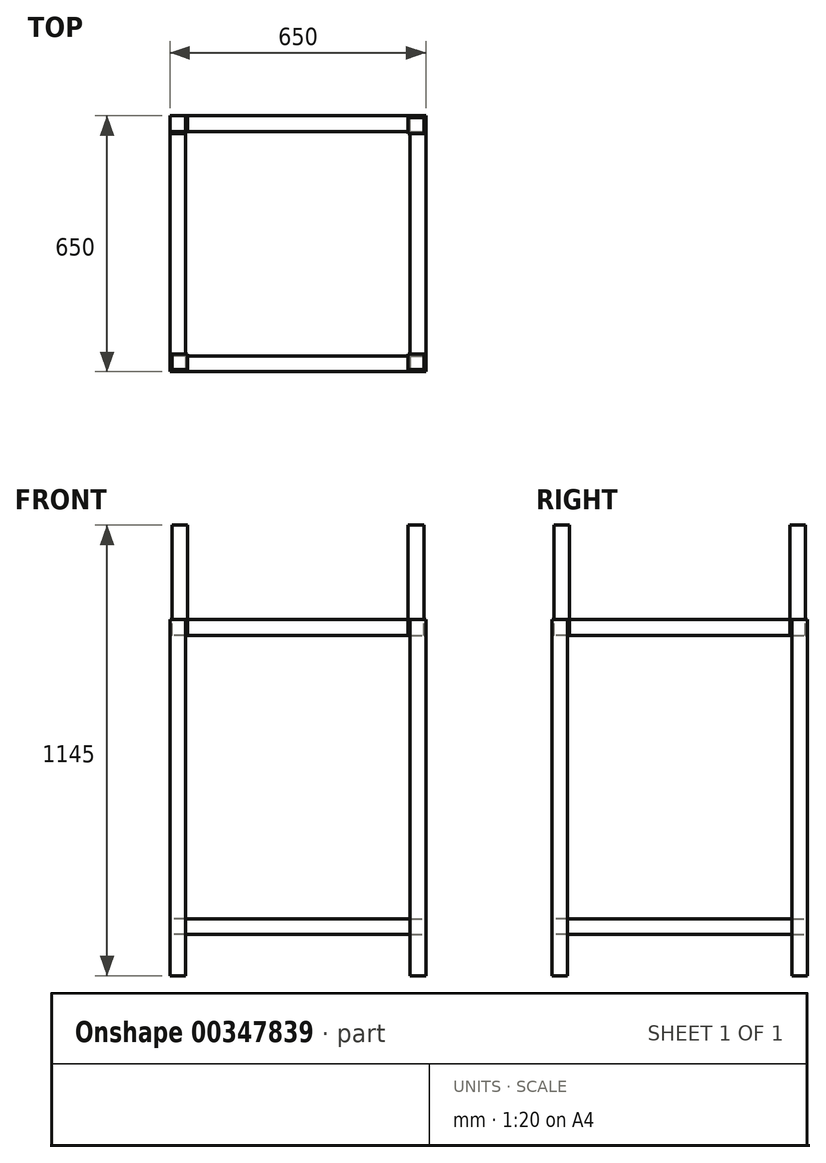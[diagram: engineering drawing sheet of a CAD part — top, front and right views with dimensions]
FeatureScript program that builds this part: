
annotation { "Feature Type Name" : "Feature", "Feature Type Description" : "" }
export const myFeature = defineFeature(function(context is Context, id is Id, definition is map)
    precondition{}
    {
        {
            var Q0;
            Q0=qCreatedBy(makeId("Top.planeOp"),FACE);
            var sketch = newSketch(context, id + "F0", { "sketchPlane" : qUnion([Q0])});
            skLineSegment(sketch, "E0.bottom", {"start": v(325, -325) * mm, "end": v(-325, -325) * mm});
            skLineSegment(sketch, "E0.top", {"start": v(325, 325) * mm, "end": v(-325, 325) * mm});
            skLineSegment(sketch, "E0.left", {"start": v(325, -325) * mm, "end": v(325, 325) * mm});
            skLineSegment(sketch, "E0.right", {"start": v(-325, -325) * mm, "end": v(-325, 325) * mm});
            skPoint(sketch, "E0.middle", {"position": v(0, 0) * mm});
            skLineSegment(sketch, "E1.0", {"start": v(285, 285) * mm, "end": v(-285, 285) * mm});
            skLineSegment(sketch, "E1.1", {"start": v(285, -285) * mm, "end": v(285, 285) * mm});
            skLineSegment(sketch, "E1.2", {"start": v(285, -285) * mm, "end": v(-285, -285) * mm});
            skLineSegment(sketch, "E1.3", {"start": v(-285, -285) * mm, "end": v(-285, 285) * mm});
            skLineSegment(sketch, "E2", {"start": v(-285, 285) * mm, "end": v(-325, 285) * mm});
            skLineSegment(sketch, "E3", {"start": v(-285, 285) * mm, "end": v(-285, 325) * mm});
            skLineSegment(sketch, "E4", {"start": v(285, 285) * mm, "end": v(285, 325) * mm});
            skLineSegment(sketch, "E5", {"start": v(285, 285) * mm, "end": v(325, 285) * mm});
            skLineSegment(sketch, "E6", {"start": v(-285, -285) * mm, "end": v(-325, -285) * mm});
            skLineSegment(sketch, "E7", {"start": v(-285, -285) * mm, "end": v(-285, -325) * mm});
            skLineSegment(sketch, "E8", {"start": v(285, -285) * mm, "end": v(325, -285) * mm});
            skLineSegment(sketch, "E9", {"start": v(285, -285) * mm, "end": v(285, -325) * mm});
            skSolve(sketch);
        }
        {
            var Q0;
            Q0=makeQuery(id+"F0.imprint","IMPRINT",FACE,{"disambiguationData":[TD([[makeQuery(id+"F0.imprint","IMPRINT",EDGE,{"derivedFrom":sQuery(id+"F0.wireOp",EDGE,"E1.0")}),-1.0]])]});
            var Q1;
            Q1=makeQuery(id+"F0.imprint","IMPRINT",FACE,{"disambiguationData":[TD([[makeQuery(id+"F0.imprint","IMPRINT",EDGE,{"derivedFrom":sQuery(id+"F0.wireOp",EDGE,"E1.3")}),1.0]])]});
            var Q2;
            Q2=makeQuery(id+"F0.imprint","IMPRINT",FACE,{"disambiguationData":[TD([[makeQuery(id+"F0.imprint","IMPRINT",EDGE,{"derivedFrom":sQuery(id+"F0.wireOp",EDGE,"E1.1")}),-1.0]])]});
            var Q3;
            Q3=makeQuery(id+"F0.imprint","IMPRINT",FACE,{"disambiguationData":[TD([[makeQuery(id+"F0.imprint","IMPRINT",EDGE,{"derivedFrom":sQuery(id+"F0.wireOp",EDGE,"E1.2")}),1.0]])]});
            extrude(context, id + "F1", {"entities" : qUnion([Q0, Q1, Q2, Q3]), "oppositeDirection" : true, "depth" : 40 * mm});
        }
        {
            var Q0;
            {var subQ4=sQuery(id+"F0.wireOp",EDGE,"E2");Q0=makeQuery(id+"F0.imprint","IMPRINT",FACE,{"disambiguationData":[TD([[makeQuery(id+"F0.imprint","IMPRINT",EDGE,{"derivedFrom":subQ4}),-1.0]])]});}
            var Q1;
            {var subQ3=sQuery(id+"F0.wireOp",EDGE,"E4");Q1=makeQuery(id+"F0.imprint","IMPRINT",FACE,{"disambiguationData":[TD([[makeQuery(id+"F0.imprint","IMPRINT",EDGE,{"derivedFrom":subQ3}),-1.0]])]});}
            var Q2;
            {var subQ4=sQuery(id+"F0.wireOp",EDGE,"E8");Q2=makeQuery(id+"F0.imprint","IMPRINT",FACE,{"disambiguationData":[TD([[makeQuery(id+"F0.imprint","IMPRINT",EDGE,{"derivedFrom":subQ4}),-1.0]])]});}
            var Q3;
            {var subQ4=sQuery(id+"F0.wireOp",EDGE,"E6");Q3=makeQuery(id+"F0.imprint","IMPRINT",FACE,{"disambiguationData":[TD([[makeQuery(id+"F0.imprint","IMPRINT",EDGE,{"derivedFrom":subQ4}),1.0]])]});}
            extrude(context, id + "F2", {"entities" : qUnion([Q0, Q1, Q2, Q3]), "depth" : 760 * mm, "hasSecondDirection" : true, "secondDirectionOppositeDirection" : true, "secondDirectionDepth" : 145 * mm});
        }
        {
            var Q0;
            Q0=makeQuery(id+"F2.opExtrude","CAP_FACE",FACE,{"disambiguationData":[OSD([sQuery(id+"F0.wireOp",EDGE,"E0.top"),sQuery(id+"F0.wireOp",EDGE,"E0.left"),sQuery(id+"F0.wireOp",EDGE,"E4"),sQuery(id+"F0.wireOp",EDGE,"E5")])],"isStart":false});
            var sketch = newSketch(context, id + "F3", { "sketchPlane" : qUnion([Q0])});
            skLineSegment(sketch, "E10.bottom", {"start": v(325, 325) * mm, "end": v(-325, 325) * mm});
            skLineSegment(sketch, "E10.top", {"start": v(325, -325) * mm, "end": v(-325, -325) * mm});
            skLineSegment(sketch, "E10.left", {"start": v(325, 325) * mm, "end": v(325, -325) * mm});
            skLineSegment(sketch, "E10.right", {"start": v(-325, 325) * mm, "end": v(-325, -325) * mm});
            skLineSegment(sketch, "E11.0", {"start": v(285, 285) * mm, "end": v(-285, 285) * mm});
            skLineSegment(sketch, "E11.1", {"start": v(285, 285) * mm, "end": v(285, -285) * mm});
            skLineSegment(sketch, "E11.2", {"start": v(285, -285) * mm, "end": v(-285, -285) * mm});
            skLineSegment(sketch, "E11.3", {"start": v(-285, 285) * mm, "end": v(-285, -285) * mm});
            skLineSegment(sketch, "E12", {"start": v(-285, 285) * mm, "end": v(-285, 325) * mm});
            skLineSegment(sketch, "E13", {"start": v(-285, 285) * mm, "end": v(-325, 285) * mm});
            skLineSegment(sketch, "E14", {"start": v(285, 285) * mm, "end": v(285, 325) * mm});
            skLineSegment(sketch, "E15", {"start": v(285, 285) * mm, "end": v(325, 285) * mm});
            skLineSegment(sketch, "E16", {"start": v(-285, -285) * mm, "end": v(-325, -285) * mm});
            skLineSegment(sketch, "E17", {"start": v(-285, -285) * mm, "end": v(-285, -325) * mm});
            skLineSegment(sketch, "E18", {"start": v(285, -285) * mm, "end": v(325, -285) * mm});
            skLineSegment(sketch, "E19", {"start": v(285, -285) * mm, "end": v(285, -325) * mm});
            skLineSegment(sketch, "E20.0", {"start": v(-280, 280) * mm, "end": v(-280, 325) * mm});
            skLineSegment(sketch, "E20.1", {"start": v(-280, 280) * mm, "end": v(-325, 280) * mm});
            skLineSegment(sketch, "E21.0", {"start": v(-320, 320) * mm, "end": v(-320, 325) * mm});
            skLineSegment(sketch, "E21.1", {"start": v(-320, 320) * mm, "end": v(-325, 320) * mm});
            skLineSegment(sketch, "E22", {"start": v(-320, 320) * mm, "end": v(-280, 320) * mm});
            skLineSegment(sketch, "E23", {"start": v(-320, 320) * mm, "end": v(-320, 280) * mm});
            skLineSegment(sketch, "E24.MirrorCS", {"start": v(320, 320) * mm, "end": v(280, 320) * mm});
            skLineSegment(sketch, "E25.MirrorCS", {"start": v(280, 280) * mm, "end": v(280, 325) * mm});
            skLineSegment(sketch, "E26.MirrorCS", {"start": v(320, 320) * mm, "end": v(320, 280) * mm});
            skLineSegment(sketch, "E27.MirrorCS", {"start": v(280, 280) * mm, "end": v(325, 280) * mm});
            skLineSegment(sketch, "E28.MirrorCS", {"start": v(-325, 325) * mm, "end": v(325, 325) * mm});
            skLineSegment(sketch, "E29.MirrorCS", {"start": v(-320, -320) * mm, "end": v(-280, -320) * mm});
            skLineSegment(sketch, "E30.MirrorCS", {"start": v(-280, -280) * mm, "end": v(-280, -325) * mm});
            skLineSegment(sketch, "E31.MirrorCS", {"start": v(-280, -280) * mm, "end": v(-325, -280) * mm});
            skLineSegment(sketch, "E32.MirrorCS", {"start": v(-320, -320) * mm, "end": v(-320, -280) * mm});
            skLineSegment(sketch, "E33.MirrorCS", {"start": v(-320, -320) * mm, "end": v(-320, -325) * mm});
            skLineSegment(sketch, "E34.MirrorCS", {"start": v(320, -320) * mm, "end": v(280, -320) * mm});
            skLineSegment(sketch, "E35.MirrorCS", {"start": v(320, -320) * mm, "end": v(320, -280) * mm});
            skLineSegment(sketch, "E36.MirrorCS", {"start": v(280, -280) * mm, "end": v(325, -280) * mm});
            skLineSegment(sketch, "E37.MirrorCS", {"start": v(280, -280) * mm, "end": v(280, -325) * mm});
            skSolve(sketch);
        }
        {
            var Q0;
            {var subQ4=sQuery(id+"F3.wireOp",EDGE,"E25.MirrorCS");var subQ6=sQuery(id+"F3.wireOp",EDGE,"E11.0");var subQ7=makeQuery(id+"F3.imprint","INTERSECT",VERTEX,{"derivedFrom":[subQ6,subQ4]});Q0=makeQuery(id+"F3.imprint","IMPRINT",FACE,{"disambiguationData":[TD([[makeQuery(id+"F3.imprint","IMPRINT",EDGE,{"disambiguationData":[TD([[subQ7,-1.0]])],"derivedFrom":subQ6}),-1.0]])]});}
            var Q1;
            {var subQ3=sQuery(id+"F3.wireOp",EDGE,"E20.0");var subQ5=sQuery(id+"F3.wireOp",EDGE,"E22");var subQ7=makeQuery(id+"F3.imprint","INTERSECT",VERTEX,{"derivedFrom":[subQ3,subQ5]});Q1=makeQuery(id+"F3.imprint","IMPRINT",FACE,{"disambiguationData":[TD([[makeQuery(id+"F3.imprint","IMPRINT",EDGE,{"disambiguationData":[TD([[subQ7,1.0]])],"derivedFrom":subQ3}),1.0]])]});}
            var Q2;
            {var subQ0=sQuery(id+"F3.wireOp",EDGE,"E28.MirrorCS");var subQ1=sQuery(id+"F3.wireOp",EDGE,"E12");var subQ2=makeQuery(id+"F3.imprint","INTERSECT",VERTEX,{"derivedFrom":[subQ1,subQ0]});Q2=makeQuery(id+"F3.imprint","IMPRINT",FACE,{"disambiguationData":[TD([[makeQuery(id+"F3.imprint","IMPRINT",EDGE,{"disambiguationData":[TD([[subQ2,1.0]])],"derivedFrom":subQ1}),-1.0]])]});}
            var Q3;
            {var subQ3=sQuery(id+"F3.wireOp",EDGE,"E20.1");var subQ5=sQuery(id+"F3.wireOp",EDGE,"E23");var subQ7=makeQuery(id+"F3.imprint","INTERSECT",VERTEX,{"derivedFrom":[subQ3,subQ5]});Q3=makeQuery(id+"F3.imprint","IMPRINT",FACE,{"disambiguationData":[TD([[makeQuery(id+"F3.imprint","IMPRINT",EDGE,{"disambiguationData":[TD([[subQ7,1.0]])],"derivedFrom":subQ3}),-1.0]])]});}
            var Q4;
            {var subQ0=sQuery(id+"F3.wireOp",EDGE,"E13");var subQ1=sQuery(id+"F3.wireOp",EDGE,"E10.right");var subQ2=makeQuery(id+"F3.imprint","INTERSECT",VERTEX,{"derivedFrom":[subQ1,subQ0]});Q4=makeQuery(id+"F3.imprint","IMPRINT",FACE,{"disambiguationData":[TD([[makeQuery(id+"F3.imprint","IMPRINT",EDGE,{"disambiguationData":[TD([[subQ2,-1.0]])],"derivedFrom":subQ1}),1.0]])]});}
            var Q5;
            {var subQ0=sQuery(id+"F3.wireOp",EDGE,"E20.1");var subQ1=sQuery(id+"F3.wireOp",EDGE,"E10.right");var subQ2=makeQuery(id+"F3.imprint","INTERSECT",VERTEX,{"derivedFrom":[subQ1,subQ0]});Q5=makeQuery(id+"F3.imprint","IMPRINT",FACE,{"disambiguationData":[TD([[makeQuery(id+"F3.imprint","IMPRINT",EDGE,{"disambiguationData":[TD([[subQ2,-1.0]])],"derivedFrom":subQ1}),1.0]])]});}
            var Q6;
            {var subQ3=sQuery(id+"F3.wireOp",EDGE,"E25.MirrorCS");var subQ5=sQuery(id+"F3.wireOp",EDGE,"E24.MirrorCS");var subQ6=makeQuery(id+"F3.imprint","INTERSECT",VERTEX,{"derivedFrom":[subQ3,subQ5]});Q6=makeQuery(id+"F3.imprint","IMPRINT",FACE,{"disambiguationData":[TD([[makeQuery(id+"F3.imprint","IMPRINT",EDGE,{"disambiguationData":[TD([[subQ6,1.0]])],"derivedFrom":subQ3}),-1.0]])]});}
            var Q7;
            {var subQ0=sQuery(id+"F3.wireOp",EDGE,"E28.MirrorCS");var subQ1=sQuery(id+"F3.wireOp",EDGE,"E14");var subQ2=makeQuery(id+"F3.imprint","INTERSECT",VERTEX,{"derivedFrom":[subQ1,subQ0]});Q7=makeQuery(id+"F3.imprint","IMPRINT",FACE,{"disambiguationData":[TD([[makeQuery(id+"F3.imprint","IMPRINT",EDGE,{"disambiguationData":[TD([[subQ2,1.0]])],"derivedFrom":subQ1}),1.0]])]});}
            var Q8;
            {var subQ3=sQuery(id+"F3.wireOp",EDGE,"E27.MirrorCS");var subQ5=sQuery(id+"F3.wireOp",EDGE,"E26.MirrorCS");var subQ7=makeQuery(id+"F3.imprint","INTERSECT",VERTEX,{"derivedFrom":[subQ5,subQ3]});Q8=makeQuery(id+"F3.imprint","IMPRINT",FACE,{"disambiguationData":[TD([[makeQuery(id+"F3.imprint","IMPRINT",EDGE,{"disambiguationData":[TD([[subQ7,1.0]])],"derivedFrom":subQ5}),-1.0]])]});}
            var Q9;
            {var subQ1=sQuery(id+"F3.wireOp",EDGE,"E10.left");var subQ3=sQuery(id+"F3.wireOp",EDGE,"E27.MirrorCS");var subQ4=makeQuery(id+"F3.imprint","INTERSECT",VERTEX,{"derivedFrom":[subQ1,subQ3]});Q9=makeQuery(id+"F3.imprint","IMPRINT",FACE,{"disambiguationData":[TD([[makeQuery(id+"F3.imprint","IMPRINT",EDGE,{"disambiguationData":[TD([[subQ4,1.0]])],"derivedFrom":subQ1}),-1.0]])]});}
            var Q10;
            {var subQ0=sQuery(id+"F3.wireOp",EDGE,"E27.MirrorCS");var subQ2=sQuery(id+"F3.wireOp",EDGE,"E10.left");var subQ3=makeQuery(id+"F3.imprint","INTERSECT",VERTEX,{"derivedFrom":[subQ2,subQ0]});Q10=makeQuery(id+"F3.imprint","IMPRINT",FACE,{"disambiguationData":[TD([[makeQuery(id+"F3.imprint","IMPRINT",EDGE,{"disambiguationData":[TD([[subQ3,-1.0]])],"derivedFrom":subQ2}),-1.0]])]});}
            var Q11;
            {var subQ3=sQuery(id+"F3.wireOp",EDGE,"E36.MirrorCS");var subQ5=sQuery(id+"F3.wireOp",EDGE,"E35.MirrorCS");var subQ6=makeQuery(id+"F3.imprint","INTERSECT",VERTEX,{"derivedFrom":[subQ5,subQ3]});Q11=makeQuery(id+"F3.imprint","IMPRINT",FACE,{"disambiguationData":[TD([[makeQuery(id+"F3.imprint","IMPRINT",EDGE,{"disambiguationData":[TD([[subQ6,1.0]])],"derivedFrom":subQ5}),1.0]])]});}
            var Q12;
            {var subQ0=sQuery(id+"F3.wireOp",EDGE,"E18");var subQ1=sQuery(id+"F3.wireOp",EDGE,"E10.left");var subQ2=makeQuery(id+"F3.imprint","INTERSECT",VERTEX,{"derivedFrom":[subQ1,subQ0]});Q12=makeQuery(id+"F3.imprint","IMPRINT",FACE,{"disambiguationData":[TD([[makeQuery(id+"F3.imprint","IMPRINT",EDGE,{"disambiguationData":[TD([[subQ2,1.0]])],"derivedFrom":subQ1}),-1.0]])]});}
            var Q13;
            {var subQ3=sQuery(id+"F3.wireOp",EDGE,"E37.MirrorCS");var subQ5=sQuery(id+"F3.wireOp",EDGE,"E34.MirrorCS");var subQ7=makeQuery(id+"F3.imprint","INTERSECT",VERTEX,{"derivedFrom":[subQ5,subQ3]});Q13=makeQuery(id+"F3.imprint","IMPRINT",FACE,{"disambiguationData":[TD([[makeQuery(id+"F3.imprint","IMPRINT",EDGE,{"disambiguationData":[TD([[subQ7,1.0]])],"derivedFrom":subQ5}),-1.0]])]});}
            var Q14;
            {var subQ0=sQuery(id+"F3.wireOp",EDGE,"E19");var subQ1=sQuery(id+"F3.wireOp",EDGE,"E10.top");var subQ2=makeQuery(id+"F3.imprint","INTERSECT",VERTEX,{"derivedFrom":[subQ1,subQ0]});Q14=makeQuery(id+"F3.imprint","IMPRINT",FACE,{"disambiguationData":[TD([[makeQuery(id+"F3.imprint","IMPRINT",EDGE,{"disambiguationData":[TD([[subQ2,-1.0]])],"derivedFrom":subQ1}),-1.0]])]});}
            var Q15;
            {var subQ0=sQuery(id+"F3.wireOp",EDGE,"E30.MirrorCS");var subQ6=sQuery(id+"F3.wireOp",EDGE,"E10.top");var subQ7=makeQuery(id+"F3.imprint","INTERSECT",VERTEX,{"derivedFrom":[subQ6,subQ0]});Q15=makeQuery(id+"F3.imprint","IMPRINT",FACE,{"disambiguationData":[TD([[makeQuery(id+"F3.imprint","IMPRINT",EDGE,{"disambiguationData":[TD([[subQ7,1.0]])],"derivedFrom":subQ6}),-1.0]])]});}
            var Q16;
            {var subQ3=sQuery(id+"F3.wireOp",EDGE,"E30.MirrorCS");var subQ5=sQuery(id+"F3.wireOp",EDGE,"E29.MirrorCS");var subQ7=makeQuery(id+"F3.imprint","INTERSECT",VERTEX,{"derivedFrom":[subQ5,subQ3]});Q16=makeQuery(id+"F3.imprint","IMPRINT",FACE,{"disambiguationData":[TD([[makeQuery(id+"F3.imprint","IMPRINT",EDGE,{"disambiguationData":[TD([[subQ7,1.0]])],"derivedFrom":subQ5}),1.0]])]});}
            var Q17;
            {var subQ0=sQuery(id+"F3.wireOp",EDGE,"E17");var subQ1=sQuery(id+"F3.wireOp",EDGE,"E10.top");var subQ2=makeQuery(id+"F3.imprint","INTERSECT",VERTEX,{"derivedFrom":[subQ1,subQ0]});Q17=makeQuery(id+"F3.imprint","IMPRINT",FACE,{"disambiguationData":[TD([[makeQuery(id+"F3.imprint","IMPRINT",EDGE,{"disambiguationData":[TD([[subQ2,1.0]])],"derivedFrom":subQ1}),-1.0]])]});}
            var Q18;
            {var subQ3=sQuery(id+"F3.wireOp",EDGE,"E31.MirrorCS");var subQ5=sQuery(id+"F3.wireOp",EDGE,"E32.MirrorCS");var subQ7=makeQuery(id+"F3.imprint","INTERSECT",VERTEX,{"derivedFrom":[subQ3,subQ5]});Q18=makeQuery(id+"F3.imprint","IMPRINT",FACE,{"disambiguationData":[TD([[makeQuery(id+"F3.imprint","IMPRINT",EDGE,{"disambiguationData":[TD([[subQ7,1.0]])],"derivedFrom":subQ3}),1.0]])]});}
            var Q19;
            {var subQ0=sQuery(id+"F3.wireOp",EDGE,"E16");var subQ1=sQuery(id+"F3.wireOp",EDGE,"E10.right");var subQ2=makeQuery(id+"F3.imprint","INTERSECT",VERTEX,{"derivedFrom":[subQ1,subQ0]});Q19=makeQuery(id+"F3.imprint","IMPRINT",FACE,{"disambiguationData":[TD([[makeQuery(id+"F3.imprint","IMPRINT",EDGE,{"disambiguationData":[TD([[subQ2,1.0]])],"derivedFrom":subQ1}),1.0]])]});}
            extrude(context, id + "F4", {"entities" : qUnion([Q0, Q1, Q2, Q3, Q4, Q5, Q6, Q7, Q8, Q9, Q10, Q11, Q12, Q13, Q14, Q15, Q16, Q17, Q18, Q19]), "oppositeDirection" : true, "depth" : 40 * mm});
        }
        {
            var Q0;
            {var subQ3=sQuery(id+"F3.wireOp",EDGE,"E36.MirrorCS");var subQ5=sQuery(id+"F3.wireOp",EDGE,"E35.MirrorCS");var subQ6=makeQuery(id+"F3.imprint","INTERSECT",VERTEX,{"derivedFrom":[subQ5,subQ3]});Q0=makeQuery(id+"F3.imprint","IMPRINT",FACE,{"disambiguationData":[TD([[makeQuery(id+"F3.imprint","IMPRINT",EDGE,{"disambiguationData":[TD([[subQ6,1.0]])],"derivedFrom":subQ5}),1.0]])]});}
            var Q1;
            {var subQ3=sQuery(id+"F3.wireOp",EDGE,"E35.MirrorCS");var subQ5=sQuery(id+"F3.wireOp",EDGE,"E34.MirrorCS");var subQ6=makeQuery(id+"F3.imprint","INTERSECT",VERTEX,{"derivedFrom":[subQ5,subQ3]});Q1=makeQuery(id+"F3.imprint","IMPRINT",FACE,{"disambiguationData":[TD([[makeQuery(id+"F3.imprint","IMPRINT",EDGE,{"disambiguationData":[TD([[subQ6,-1.0]])],"derivedFrom":subQ5}),-1.0]])]});}
            var Q2;
            {var subQ3=sQuery(id+"F3.wireOp",EDGE,"E37.MirrorCS");var subQ5=sQuery(id+"F3.wireOp",EDGE,"E34.MirrorCS");var subQ7=makeQuery(id+"F3.imprint","INTERSECT",VERTEX,{"derivedFrom":[subQ5,subQ3]});Q2=makeQuery(id+"F3.imprint","IMPRINT",FACE,{"disambiguationData":[TD([[makeQuery(id+"F3.imprint","IMPRINT",EDGE,{"disambiguationData":[TD([[subQ7,1.0]])],"derivedFrom":subQ5}),-1.0]])]});}
            var Q3;
            {var subQ3=sQuery(id+"F3.wireOp",EDGE,"E36.MirrorCS");var subQ5=sQuery(id+"F3.wireOp",EDGE,"E37.MirrorCS");var subQ7=makeQuery(id+"F3.imprint","INTERSECT",VERTEX,{"derivedFrom":[subQ3,subQ5]});Q3=makeQuery(id+"F3.imprint","IMPRINT",FACE,{"disambiguationData":[TD([[makeQuery(id+"F3.imprint","IMPRINT",EDGE,{"disambiguationData":[TD([[subQ7,-1.0]])],"derivedFrom":subQ3}),-1.0]])]});}
            var Q4;
            {var subQ3=sQuery(id+"F3.wireOp",EDGE,"E24.MirrorCS");var subQ5=sQuery(id+"F3.wireOp",EDGE,"E26.MirrorCS");var subQ7=makeQuery(id+"F3.imprint","INTERSECT",VERTEX,{"derivedFrom":[subQ5,subQ3]});Q4=makeQuery(id+"F3.imprint","IMPRINT",FACE,{"disambiguationData":[TD([[makeQuery(id+"F3.imprint","IMPRINT",EDGE,{"disambiguationData":[TD([[subQ7,-1.0]])],"derivedFrom":subQ5}),-1.0]])]});}
            var Q5;
            {var subQ3=sQuery(id+"F3.wireOp",EDGE,"E27.MirrorCS");var subQ5=sQuery(id+"F3.wireOp",EDGE,"E26.MirrorCS");var subQ7=makeQuery(id+"F3.imprint","INTERSECT",VERTEX,{"derivedFrom":[subQ5,subQ3]});Q5=makeQuery(id+"F3.imprint","IMPRINT",FACE,{"disambiguationData":[TD([[makeQuery(id+"F3.imprint","IMPRINT",EDGE,{"disambiguationData":[TD([[subQ7,1.0]])],"derivedFrom":subQ5}),-1.0]])]});}
            var Q6;
            {var subQ3=sQuery(id+"F3.wireOp",EDGE,"E25.MirrorCS");var subQ5=sQuery(id+"F3.wireOp",EDGE,"E27.MirrorCS");var subQ6=makeQuery(id+"F3.imprint","INTERSECT",VERTEX,{"derivedFrom":[subQ3,subQ5]});Q6=makeQuery(id+"F3.imprint","IMPRINT",FACE,{"disambiguationData":[TD([[makeQuery(id+"F3.imprint","IMPRINT",EDGE,{"disambiguationData":[TD([[subQ6,-1.0]])],"derivedFrom":subQ3}),-1.0]])]});}
            var Q7;
            {var subQ3=sQuery(id+"F3.wireOp",EDGE,"E25.MirrorCS");var subQ5=sQuery(id+"F3.wireOp",EDGE,"E24.MirrorCS");var subQ6=makeQuery(id+"F3.imprint","INTERSECT",VERTEX,{"derivedFrom":[subQ3,subQ5]});Q7=makeQuery(id+"F3.imprint","IMPRINT",FACE,{"disambiguationData":[TD([[makeQuery(id+"F3.imprint","IMPRINT",EDGE,{"disambiguationData":[TD([[subQ6,1.0]])],"derivedFrom":subQ3}),-1.0]])]});}
            var Q8;
            {var subQ0=sQuery(id+"F3.wireOp",EDGE,"E17");var subQ5=sQuery(id+"F3.wireOp",EDGE,"E29.MirrorCS");var subQ6=makeQuery(id+"F3.imprint","INTERSECT",VERTEX,{"derivedFrom":[subQ0,subQ5]});Q8=makeQuery(id+"F3.imprint","IMPRINT",FACE,{"disambiguationData":[TD([[makeQuery(id+"F3.imprint","IMPRINT",EDGE,{"disambiguationData":[TD([[subQ6,1.0]])],"derivedFrom":subQ5}),1.0]])]});}
            var Q9;
            {var subQ3=sQuery(id+"F3.wireOp",EDGE,"E31.MirrorCS");var subQ5=sQuery(id+"F3.wireOp",EDGE,"E32.MirrorCS");var subQ7=makeQuery(id+"F3.imprint","INTERSECT",VERTEX,{"derivedFrom":[subQ3,subQ5]});Q9=makeQuery(id+"F3.imprint","IMPRINT",FACE,{"disambiguationData":[TD([[makeQuery(id+"F3.imprint","IMPRINT",EDGE,{"disambiguationData":[TD([[subQ7,1.0]])],"derivedFrom":subQ3}),1.0]])]});}
            var Q10;
            {var subQ3=sQuery(id+"F3.wireOp",EDGE,"E30.MirrorCS");var subQ5=sQuery(id+"F3.wireOp",EDGE,"E31.MirrorCS");var subQ6=makeQuery(id+"F3.imprint","INTERSECT",VERTEX,{"derivedFrom":[subQ3,subQ5]});Q10=makeQuery(id+"F3.imprint","IMPRINT",FACE,{"disambiguationData":[TD([[makeQuery(id+"F3.imprint","IMPRINT",EDGE,{"disambiguationData":[TD([[subQ6,-1.0]])],"derivedFrom":subQ3}),-1.0]])]});}
            var Q11;
            {var subQ3=sQuery(id+"F3.wireOp",EDGE,"E30.MirrorCS");var subQ5=sQuery(id+"F3.wireOp",EDGE,"E29.MirrorCS");var subQ7=makeQuery(id+"F3.imprint","INTERSECT",VERTEX,{"derivedFrom":[subQ5,subQ3]});Q11=makeQuery(id+"F3.imprint","IMPRINT",FACE,{"disambiguationData":[TD([[makeQuery(id+"F3.imprint","IMPRINT",EDGE,{"disambiguationData":[TD([[subQ7,1.0]])],"derivedFrom":subQ5}),1.0]])]});}
            extrude(context, id + "F5", {"entities" : qUnion([Q0, Q1, Q2, Q3, Q4, Q5, Q6, Q7, Q8, Q9, Q10, Q11]), "depth" : 240 * mm});
        }
    });
